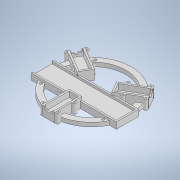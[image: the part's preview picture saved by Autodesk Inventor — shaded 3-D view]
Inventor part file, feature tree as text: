
AUTODESK INVENTOR PART (.ipt)
format: ipt  version: 2020.4 (Build 244396000, 396)  size: 497,152 bytes
history: native  units: mm
features: sketch x7, extrude x6, pattern_circular x1, hole x1, projected_geometry x1
ambient origin geometry x8: Origin, YZ Plane, XZ Plane, XY Plane, X Axis, Y Axis, Z Axis, Center Point
bodies: Solid1 (feature_tree)
feature tree (16):
  extrude  "Extrusion1"  Depth=86.0mm
  extrude  "Extrusion5"  Depth=7.0mm TaperAngle=0.0deg
  extrude  "Extrusion14"  Depth=9.0mm
  extrude  "Extrusion15"  Depth=2.0mm
  pattern_circular  "Circular Pattern3"  [2 undecoded]
  hole  "Hole1"  [1 undecoded]
  extrude  "Extrusion16"  Depth=0.5mm
  extrude  "Extrusion17"  Depth=0.5mm
  sketch  "Sketch1"  dims[d0=100.0mm d1=86.0mm]
  sketch  "Sketch6"  dims[d20=5.0mm d21=0.0mm d48=7.0mm d49=0.0mm]
  sketch  "Sketch7"  dims[d51=5.0mm d53=9.0mm]
  sketch  "Sketch11"  dims[d54=2.0mm d55=2.0mm]
  projected_geometry  "Projected Loop2"
  sketch  "Sketch16"  dims[d61=93.0mm]
  sketch  "Sketch17"  dims[d62=3.0mm]
  sketch  "Sketch18"  dims[d63=3.0mm d64=3.0mm d65=3.0mm d66=35.0mm d67=35.0mm d68=25.0mm d69=25.0mm d95=30.0mm d96=360.0deg d119=3.2mm d120=6.0mm d121=18.0mm d122=4.8mm d123=90.0deg d124=5.0mm d125=20.594885mm d147=12.0mm d148=30.0mm d149=2.0mm d150=30.0mm d152=360.0deg d154=24.0mm d156=2.0mm d157=10.0mm d158=0.0mm d159=5.0mm d162=25.8mm d163=2.0mm d164=1.5mm d165=16.0mm d166=20.0mm d168=18.0mm d169=20.0mm d171=21.0mm d174=10.0mm d175=0.0mm d176=103.0mm d177=24.0mm d178=2.0mm d179=3.0mm d180=10.0mm d181=0.0mm d182=2.0mm d183=3.0mm d184=0.0mm d126=0.5mm d127=0.872665mm d128=0.5mm d129=0.872665mm]
note: 3 required parameter values undecoded (feature->parameter linkage not recoverable at this tier; creation-order binding heuristic only, values carry confidence <= 0.55)
